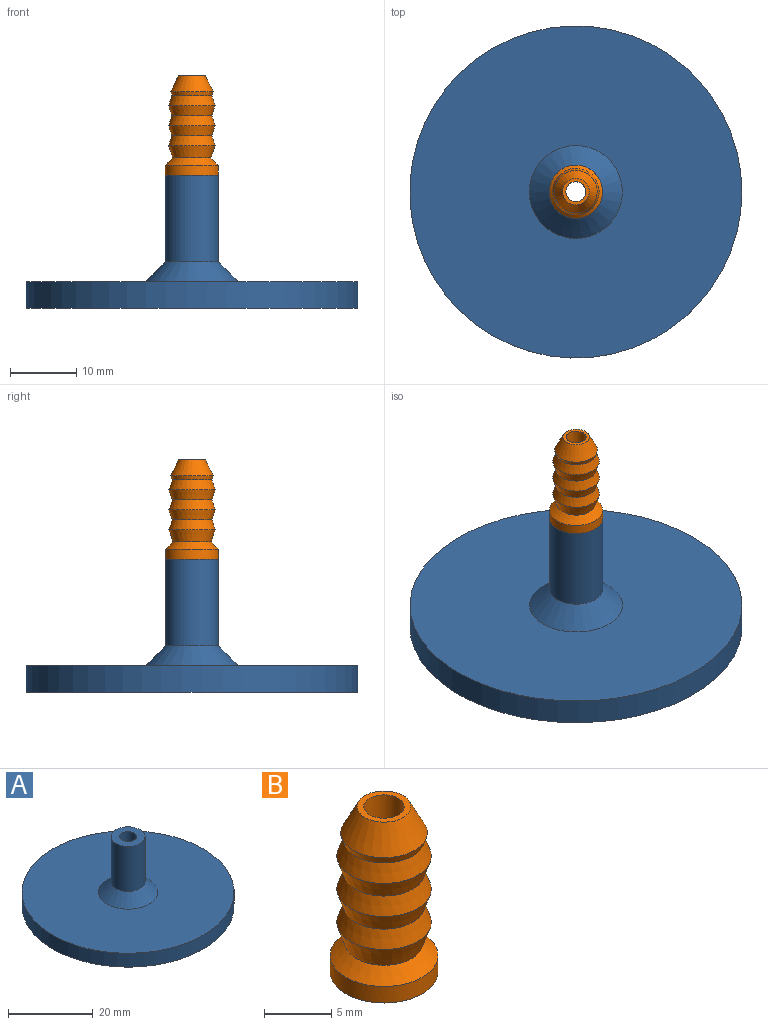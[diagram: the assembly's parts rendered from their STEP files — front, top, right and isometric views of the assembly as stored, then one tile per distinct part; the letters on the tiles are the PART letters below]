
ASSEMBLY  parts=2 mates=1
PART A: 8 faces, bbox 50x50x20 mm
  f0: cylinder r=25mm len=50mm, axis (0,0,-1), area 628.3mm2, adj f1,f2
  f1: plane 50x50mm, normal (0,0,1), area 1809.6mm2, adj f0,f6
  f2: plane 50x50mm, normal (0,0,-1), area 1935.2mm2, adj f0,f7
  f3: cylinder r=2mm len=19mm, axis (0,0,-1), area 238.8mm2, adj f5,f7
  f4: cylinder r=4mm len=13mm, axis (0,0,-1), area 326.7mm2, adj f5,f6
  f5: plane 8x8mm, normal (0,0,1), area 37.7mm2, adj f3,f4
  f6: cone r=4mm half-angle=45deg, axis (0,0,-1), area 146.6mm2, adj f1,f4
  f7: cone r=3mm half-angle=45deg, axis (0,0,-1), area 22.2mm2, adj f2,f3
PART B: 14 faces, bbox 8x8x15 mm
  f0: cylinder r=4mm len=8mm, axis (0,0,1), area 37.7mm2, adj f2,f11
  f1: cylinder r=1.5mm len=14.2mm, axis (0,0,1), area 133.8mm2, adj f3,f12
  f2: plane 8x8mm, normal (0,0,-1), area 33.6mm2, adj f0,f12
  f3: plane 4x4mm, normal (0,0,1), area 5.5mm2, adj f1,f13
  f4: cone r=3.5mm half-angle=18.4deg, axis (0,0,1), area 12.9mm2, adj f6,f13
  f5: cone r=3.5mm half-angle=18.4deg, axis (0,0,1), area 32.3mm2, adj f6,f8
  f6: cone r=3mm half-angle=18.4deg, axis (0,0,-1), area 32.3mm2, adj f4,f5
  f7: cone r=3.5mm half-angle=18.4deg, axis (0,0,1), area 32.3mm2, adj f8,f10
  f8: cone r=3mm half-angle=18.4deg, axis (0,0,-1), area 32.3mm2, adj f5,f7
  f9: cone r=3.5mm half-angle=18.4deg, axis (0,0,1), area 39.6mm2, adj f10,f11
  f10: cone r=3mm half-angle=18.4deg, axis (0,0,-1), area 32.3mm2, adj f7,f9
  f11: cone r=2.5mm half-angle=45deg, axis (0,0,-1), area 34.4mm2, adj f0,f9
  f12: cone r=2.3mm half-angle=45deg, axis (0,0,-1), area 13.5mm2, adj f1,f2
  f13: cone r=4.9mm half-angle=27deg, axis (0,0,-1), area 43.6mm2, adj f3,f4
PLACE A t=(-0.22,-0.05,-14.89)mm
PLACE B t=(-0.22,-0.05,8.11)mm
MATE fastened B.f0 <-> A.f4  axis (0,0,-1) through (-0.22,-0.05,5.11)mm
